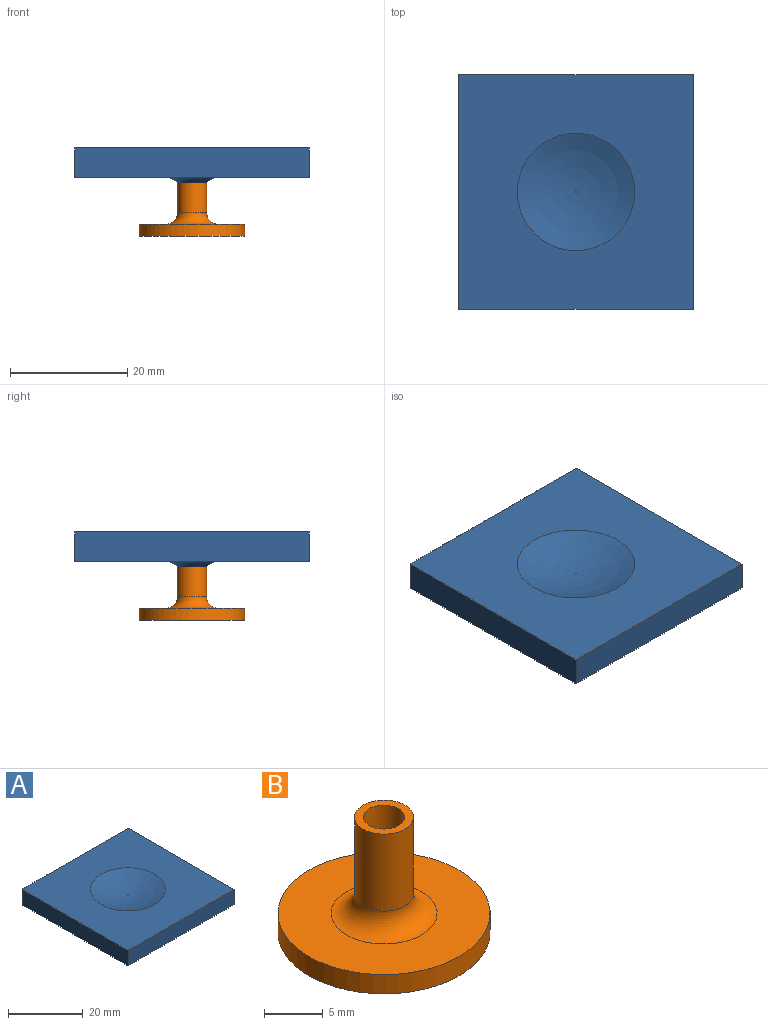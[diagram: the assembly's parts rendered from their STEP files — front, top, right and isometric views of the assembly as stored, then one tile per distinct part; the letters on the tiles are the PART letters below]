
ASSEMBLY  parts=2 mates=1
PART A: 11 faces, bbox 40x40x11 mm
  f0: plane 40x5mm, normal (-1,0,0), area 200mm2, adj f1,f3,f4,f5
  f1: plane 40x5mm, normal (0,-1,0), area 200mm2, adj f0,f2,f4,f5
  f2: plane 40x5mm, normal (1,0,0), area 200mm2, adj f1,f3,f4,f5
  f3: plane 40x5mm, normal (0,1,0), area 200mm2, adj f0,f2,f4,f5
  f4: plane 40x40mm, normal (0,0,1), area 1285.8mm2, adj f0,f1,f2,f3,f7
  f5: plane 40x40mm, normal (0,0,-1), area 1532.1mm2, adj f0,f1,f2,f3,f10
  f6: plane 0.2x0.2mm, normal (0,0,1), area 0mm2, adj f7
  f7: torus R=0.1mm, axis (0,0,-1), area 326.9mm2, adj f4,f6
  f8: cylinder r=1.65mm len=3.3mm, axis (0,0,1), area 31.1mm2, adj f9,f10
  f9: plane 3.3x3.3mm, normal (0,0,-1), area 8.6mm2, adj f8
  f10: torus R=4.65mm, axis (0,0,1), area 81.1mm2, adj f5,f8
PART B: 8 faces, bbox 18x18x12 mm
  f0: cylinder r=9mm len=18mm, axis (0,0,-1), area 113.1mm2, adj f1,f2
  f1: plane 18x18mm, normal (0,0,1), area 190.9mm2, adj f0,f5
  f2: plane 18x18mm, normal (0,0,-1), area 254.5mm2, adj f0
  f3: cylinder r=2.5mm len=8mm, axis (0,0,-1), area 125.7mm2, adj f4,f5
  f4: plane 5x5mm, normal (0,0,1), area 10mm2, adj f3,f6
  f5: torus R=4.5mm, axis (0,0,1), area 63.7mm2, adj f1,f3
  f6: cylinder r=1.75mm len=6mm, axis (0,0,1), area 66mm2, adj f4,f7
  f7: plane 3.5x3.5mm, normal (0,0,1), area 9.6mm2, adj f6
PLACE A t=(-22.34,-31.87,32.28)mm
PLACE B t=(-2.34,-11.87,22.28)mm
MATE slider A.f7 <-> B.f3  axis (0,0,1) through (-2.34,-11.87,26.28)mm
